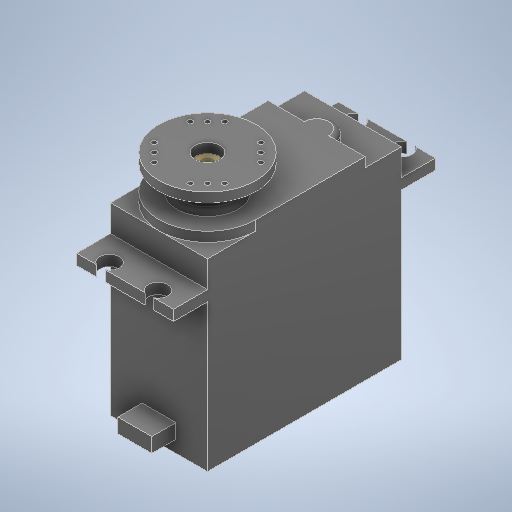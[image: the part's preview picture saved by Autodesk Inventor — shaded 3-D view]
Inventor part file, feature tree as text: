
AUTODESK INVENTOR PART (.ipt)
format: ipt  version: 2025.2 (Build 292293000, 293)  size: 332,288 bytes
history: native  units: mm
features: extrude x3, other x2, sketch x1, pattern_circular x1
ambient origin geometry x8: Origin, YZ Plane, XZ Plane, XY Plane, X Axis, Y Axis, Z Axis, Center Point
bodies: Body1 (feature_tree)
feature tree (7):
  other  "Sólido1"
  sketch  "Esboço1"  dims[d0=20.0mm d1=2.0mm d2=0.0mm d3=45.0deg d4=1.0mm d5=5.0mm d6=5.5mm d7=90.0deg d8=0.0mm d9=0.0mm d10=40.0mm d11=360.0deg d13=5.05mm d14=2.0mm d15=0.0mm d16=0.5mm d17=0.872665mm]
  extrude  "Extrusão1"  Depth=2.0mm TaperAngle=0.0deg
  extrude  "Extrusão2"  TaperAngle=45.0deg  [1 undecoded]
  pattern_circular  "Padrão circular1"  [2 undecoded]
  extrude  "Extrusão3"  Depth=5.0mm
  other  "Cut-Extrude2"
note: 3 required parameter values undecoded (feature->parameter linkage not recoverable at this tier; creation-order binding heuristic only, values carry confidence <= 0.55)
